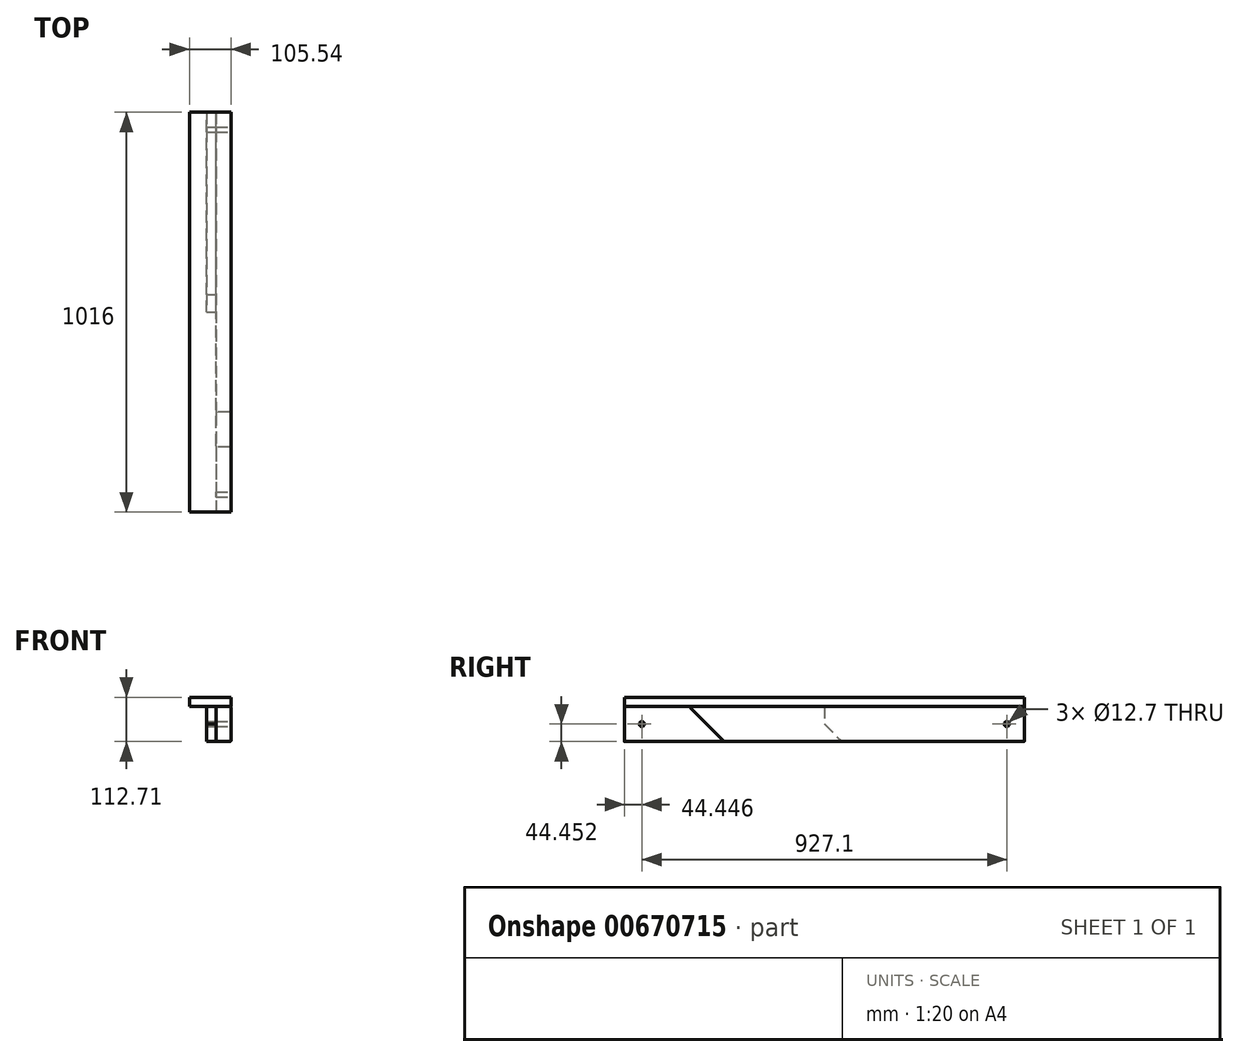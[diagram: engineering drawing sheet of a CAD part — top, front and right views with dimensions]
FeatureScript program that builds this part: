
annotation { "Feature Type Name" : "Feature", "Feature Type Description" : "" }
export const myFeature = defineFeature(function(context is Context, id is Id, definition is map)
    precondition{}
    {
        {
            var Q0;
            Q0=qCreatedBy(makeId("Right.planeOp"),FACE);
            var sketch = newSketch(context, id + "F0", { "sketchPlane" : qUnion([Q0])});
            skLineSegment(sketch, "E0", {"start": v(-267.3, 45.07) * mm, "end": v(583.6, 45.07) * mm});
            skLineSegment(sketch, "E1", {"start": v(583.6, 45.07) * mm, "end": v(583.6, -43.83) * mm});
            skLineSegment(sketch, "E2", {"start": v(583.6, -43.83) * mm, "end": v(-178.4, -43.83) * mm});
            skLineSegment(sketch, "E3", {"start": v(-178.4, -43.83) * mm, "end": v(-267.3, 45.07) * mm});
            skSolve(sketch);
        }
        {
            var Q0;
            Q0=makeQuery(id+"F0.imprint","IMPRINT",FACE,{"disambiguationData":[TD([[makeQuery(id+"F0.imprint","IMPRINT",EDGE,{"derivedFrom":sQuery(id+"F0.wireOp",EDGE,"E0")}),-1.0]])]});
            extrude(context, id + "F1", {"entities" : qUnion([Q0]), "depth" : 38.1 * mm, "offsetDistance" : 25.4 * mm});
        }
        {
            var Q0;
            Q0=makeQuery(id+"F1.opExtrude","CAP_EDGE",EDGE,{"disambiguationData":[OSD([sQuery(id+"F0.wireOp",EDGE,"E0")])],"isStart":false});
            var Q1;
            Q1=makeQuery(id+"F1.opExtrude","CAP_EDGE",EDGE,{"disambiguationData":[OSD([sQuery(id+"F0.wireOp",EDGE,"E0")])],"isStart":true});
            var Q2;
            Q2=makeQuery(id+"F1.opExtrude","CAP_EDGE",EDGE,{"disambiguationData":[OSD([sQuery(id+"F0.wireOp",EDGE,"E2")])],"isStart":false});
            var Q3;
            Q3=makeQuery(id+"F1.opExtrude","CAP_EDGE",EDGE,{"disambiguationData":[OSD([sQuery(id+"F0.wireOp",EDGE,"E2")])],"isStart":true});
            fillet(context, id + "F2", {"entities" : qUnion([Q0, Q1, Q2, Q3]), "radius" : 3.17 * mm, "tangentPropagation" : true, "allowEdgeOverflow" : false});
        }
        {
            var Q0;
            Q0=qCreatedBy(makeId("Right.planeOp"),FACE);
            var sketch = newSketch(context, id + "F3", { "sketchPlane" : qUnion([Q0])});
            skPoint(sketch, "E4.0", {"position": v(-267.3, 45.07) * mm});
            skPoint(sketch, "E5.0", {"position": v(-178.4, -43.83) * mm});
            skLineSegment(sketch, "E6", {"start": v(-178.4, -43.83) * mm, "end": v(-432.4, -43.83) * mm});
            skLineSegment(sketch, "E7", {"start": v(-267.3, 45.07) * mm, "end": v(-432.4, 45.07) * mm});
            skLineSegment(sketch, "E8", {"start": v(-432.4, 45.07) * mm, "end": v(-432.4, -43.83) * mm});
            skLineSegment(sketch, "E9", {"start": v(-267.3, 45.07) * mm, "end": v(-178.4, -43.83) * mm});
            skSolve(sketch);
        }
        {
            var Q0;
            Q0=makeQuery(id+"F3.imprint","IMPRINT",FACE,{"disambiguationData":[TD([[makeQuery(id+"F3.imprint","IMPRINT",EDGE,{"derivedFrom":sQuery(id+"F3.wireOp",EDGE,"E6")}),-1.0]])]});
            extrude(context, id + "F4", {"entities" : qUnion([Q0]), "depth" : 38.1 * mm, "offsetDistance" : 25.4 * mm});
        }
        {
            var Q0;
            Q0=makeQuery(id+"F4.opExtrude","CAP_EDGE",EDGE,{"disambiguationData":[OSD([sQuery(id+"F3.wireOp",EDGE,"E7")])],"isStart":false});
            var Q1;
            Q1=makeQuery(id+"F4.opExtrude","CAP_EDGE",EDGE,{"disambiguationData":[OSD([sQuery(id+"F3.wireOp",EDGE,"E7")])],"isStart":true});
            var Q2;
            Q2=makeQuery(id+"F4.opExtrude","CAP_EDGE",EDGE,{"disambiguationData":[OSD([sQuery(id+"F3.wireOp",EDGE,"E6")])],"isStart":false});
            var Q3;
            Q3=makeQuery(id+"F4.opExtrude","CAP_EDGE",EDGE,{"disambiguationData":[OSD([sQuery(id+"F3.wireOp",EDGE,"E6")])],"isStart":true});
            fillet(context, id + "F5", {"entities" : qUnion([Q0, Q1, Q2, Q3]), "radius" : 3.17 * mm, "tangentPropagation" : true, "allowEdgeOverflow" : false});
        }
        {
            var Q0;
            Q0=qCreatedBy(makeId("Right.planeOp"),FACE);
            var sketch = newSketch(context, id + "F6", { "sketchPlane" : qUnion([Q0])});
            skPoint(sketch, "E10.0", {"position": v(583.6, 45.07) * mm});
            skPoint(sketch, "E11.0", {"position": v(583.6, -43.83) * mm});
            skLineSegment(sketch, "E12", {"start": v(583.6, 45.07) * mm, "end": v(75.6, 45.07) * mm});
            skLineSegment(sketch, "E13", {"start": v(75.6, 45.07) * mm, "end": v(75.6, 0.62) * mm});
            skLineSegment(sketch, "E14", {"start": v(75.6, 0.62) * mm, "end": v(120.06, -43.83) * mm});
            skLineSegment(sketch, "E15", {"start": v(120.06, -43.83) * mm, "end": v(583.6, -43.83) * mm});
            skLineSegment(sketch, "E16", {"start": v(583.6, 45.07) * mm, "end": v(583.6, -43.83) * mm});
            skSolve(sketch);
        }
        {
            var Q0;
            Q0 = qSketchRegion(id + "F6", true);
            extrude(context, id + "F7", {"entities" : qUnion([Q0]), "oppositeDirection" : true, "depth" : 23.8 * mm, "offsetDistance" : 25.4 * mm});
        }
        {
            var Q0;
            Q0=makeQuery(id+"F1.opExtrude","SWEPT_FACE",FACE,{"disambiguationData":[OSD([sQuery(id+"F0.wireOp",EDGE,"E0")])]});
            cPlane(context, id + "F8", {"entities" : qUnion([Q0]), "cplaneType" : CPlaneType.OFFSET, "offset" : 0 * mm, "width" : 152.4 * mm, "height" : 152.4 * mm});
        }
        {
            var Q0;
            Q0=qCreatedBy(id+"F8.planeOp",FACE);
            var sketch = newSketch(context, id + "F9", { "sketchPlane" : qUnion([Q0])});
            skPoint(sketch, "E17.0", {"position": v(38.1, 583.6) * mm});
            skPoint(sketch, "E18.0", {"position": v(38.1, -432.4) * mm});
            skLineSegment(sketch, "E19", {"start": v(38.1, -432.4) * mm, "end": v(38.1, 583.6) * mm});
            skLineSegment(sketch, "E20", {"start": v(-67.44, 583.6) * mm, "end": v(38.1, 583.6) * mm});
            skLineSegment(sketch, "E21", {"start": v(38.1, -432.4) * mm, "end": v(-67.44, -432.4) * mm});
            skLineSegment(sketch, "E22", {"start": v(-67.44, -432.4) * mm, "end": v(-67.44, 583.6) * mm});
            skSolve(sketch);
        }
        {
            var Q0;
            Q0=makeQuery(id+"F9.imprint","IMPRINT",FACE,{"disambiguationData":[TD([[makeQuery(id+"F9.imprint","IMPRINT",EDGE,{"derivedFrom":sQuery(id+"F9.wireOp",EDGE,"E19")}),1.0]])]});
            extrude(context, id + "F10", {"entities" : qUnion([Q0]), "depth" : 23.8 * mm, "offsetDistance" : 25.4 * mm});
        }
        {
            var Q0;
            Q0=qCreatedBy(makeId("Right.planeOp"),FACE);
            var sketch = newSketch(context, id + "F11", { "sketchPlane" : qUnion([Q0])});
            skCircle(sketch, "E23", {"center": v(-387.94, 0.62) * mm, "radius": 6.35 * mm});
            skCircle(sketch, "E24", {"center": v(539.16, 0.62) * mm, "radius": 6.35 * mm});
            skSolve(sketch);
        }
        {
            var Q0;
            Q0 = qSketchRegion(id + "F11", true);
            extrude(context, id + "F12", {"entities" : qUnion([Q0]), "operationType" : NewBodyOperationType.REMOVE, "endBound" : BoundingType.THROUGH_ALL, "oppositeDirection" : true, "depth" : 25.4 * mm, "offsetDistance" : 25.4 * mm, "hasSecondDirection" : true, "secondDirectionBound" : SecondDirectionBoundingType.THROUGH_ALL, "secondDirectionOppositeDirection" : false, "secondDirectionDepth" : 25.4 * mm});
        }
    });
